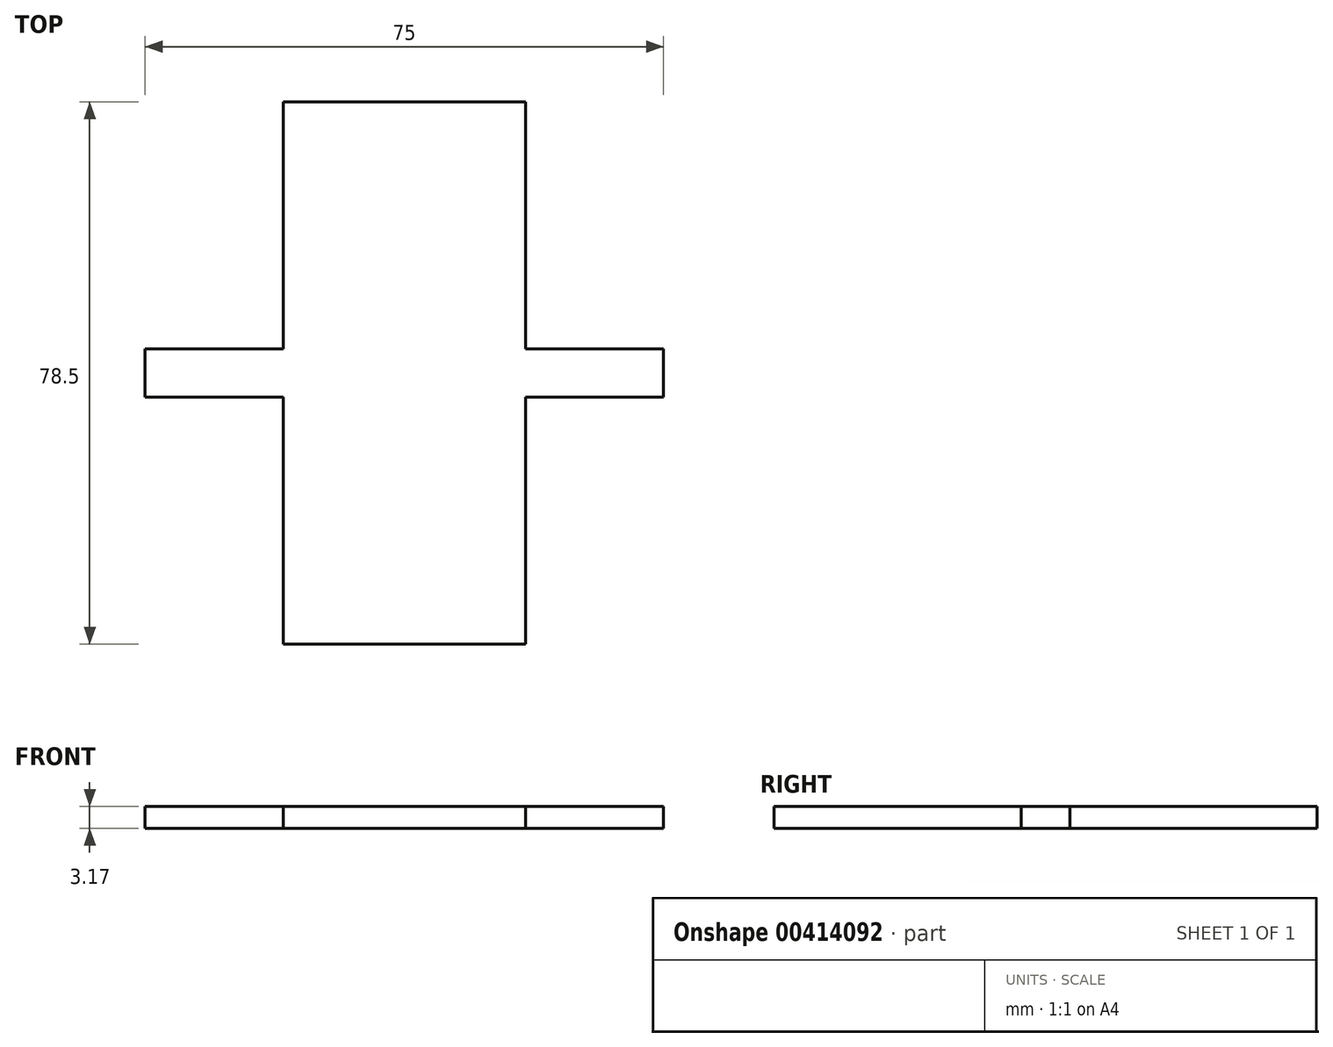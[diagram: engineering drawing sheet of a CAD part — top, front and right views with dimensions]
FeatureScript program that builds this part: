
annotation { "Feature Type Name" : "Feature", "Feature Type Description" : "" }
export const myFeature = defineFeature(function(context is Context, id is Id, definition is map)
    precondition{}
    {
        {
            var Q0;
            Q0=qCreatedBy(makeId("Top.planeOp"),FACE);
            var sketch = newSketch(context, id + "F0", { "sketchPlane" : qUnion([Q0])});
            skLineSegment(sketch, "E0.bottom", {"start": v(0, 0) * mm, "end": v(35, 0) * mm});
            skLineSegment(sketch, "E0.top", {"start": v(0, 78.5) * mm, "end": v(35, 78.5) * mm});
            skLineSegment(sketch, "E0.left", {"start": v(0, 0) * mm, "end": v(0, 35.75) * mm});
            skLineSegment(sketch, "E0.right", {"start": v(35, 0) * mm, "end": v(35, 35.75) * mm});
            skLineSegment(sketch, "E1.top", {"start": v(-20, 35.75) * mm, "end": v(0, 35.75) * mm});
            skLineSegment(sketch, "E1.left", {"start": v(-20, 39.25) * mm, "end": v(-20, 35.75) * mm});
            skLineSegment(sketch, "E2.top", {"start": v(-20, 42.75) * mm, "end": v(0, 42.75) * mm});
            skLineSegment(sketch, "E2.left", {"start": v(-20, 39.25) * mm, "end": v(-20, 42.75) * mm});
            skLineSegment(sketch, "E3.top", {"start": v(55, 42.75) * mm, "end": v(35, 42.75) * mm});
            skLineSegment(sketch, "E3.left", {"start": v(55, 39.25) * mm, "end": v(55, 42.75) * mm});
            skLineSegment(sketch, "E4.top", {"start": v(55, 35.75) * mm, "end": v(35, 35.75) * mm});
            skLineSegment(sketch, "E4.left", {"start": v(55, 39.25) * mm, "end": v(55, 35.75) * mm});
            skLineSegment(sketch, "E5.trimOffspring", {"start": v(0, 42.75) * mm, "end": v(0, 78.5) * mm});
            skPoint(sketch, "E6.orphan", {"position": v(0, 39.25) * mm});
            skLineSegment(sketch, "E7.trimOffspring", {"start": v(35, 42.75) * mm, "end": v(35, 78.5) * mm});
            skPoint(sketch, "E8.start.orphan", {"position": v(35, 39.25) * mm});
            skSolve(sketch);
        }
        {
            var Q0;
            Q0=makeQuery(id+"F0.imprint","IMPRINT",FACE,{"disambiguationData":[TD([[makeQuery(id+"F0.imprint","IMPRINT",EDGE,{"derivedFrom":sQuery(id+"F0.wireOp",EDGE,"E0.bottom")}),1.0]])]});
            extrude(context, id + "F1", {"entities" : qUnion([Q0]), "depth" : 3.17 * mm});
        }
    });
